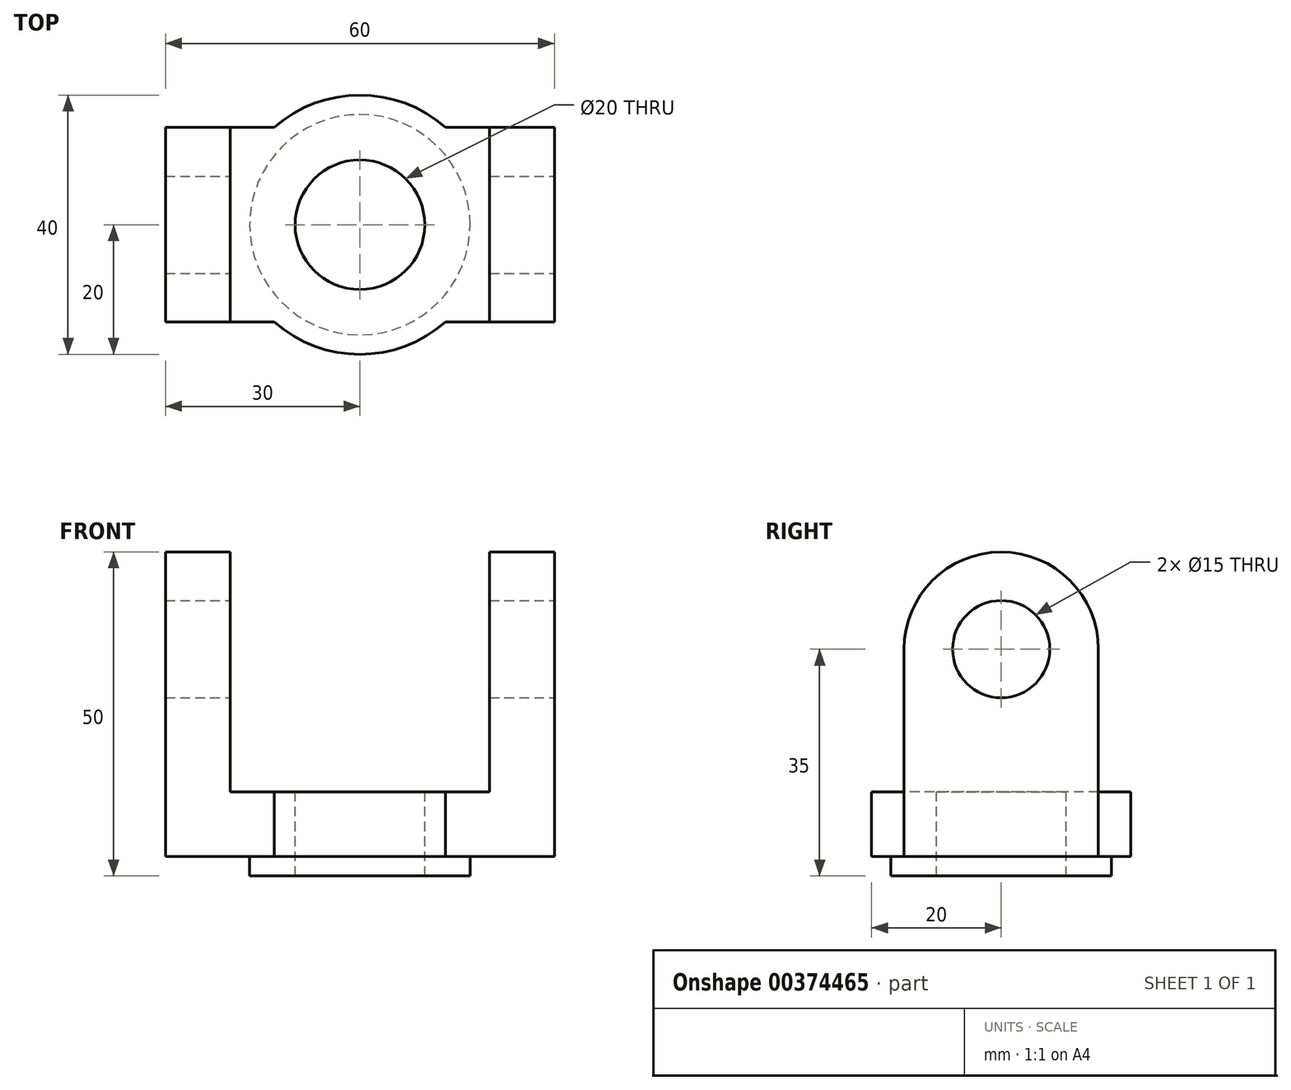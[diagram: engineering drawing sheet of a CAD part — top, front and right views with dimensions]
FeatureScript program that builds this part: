
annotation { "Feature Type Name" : "Feature", "Feature Type Description" : "" }
export const myFeature = defineFeature(function(context is Context, id is Id, definition is map)
    precondition{}
    {
        {
            var Q0;
            Q0=qCreatedBy(makeId("Front.planeOp"),FACE);
            var sketch = newSketch(context, id + "F0", { "sketchPlane" : qUnion([Q0])});
            skLineSegment(sketch, "E0", {"start": v(0, 0) * mm, "end": v(60, 0) * mm});
            skLineSegment(sketch, "E1", {"start": v(60, 0) * mm, "end": v(60, 10) * mm});
            skLineSegment(sketch, "E2", {"start": v(60, 10) * mm, "end": v(0, 10) * mm});
            skLineSegment(sketch, "E3", {"start": v(0, 10) * mm, "end": v(0, 0) * mm});
            skSolve(sketch);
        }
        {
            var Q0;
            Q0 = qSketchRegion(id + "F0", true);
            extrude(context, id + "F1", {"entities" : qUnion([Q0]), "depth" : 30 * mm});
        }
        {
            var Q0;
            Q0=makeQuery(id+"F1.opExtrude","SWEPT_FACE",FACE,{"disambiguationData":[OSD([sQuery(id+"F0.wireOp",EDGE,"E0")])]});
            var sketch = newSketch(context, id + "F2", { "sketchPlane" : qUnion([Q0])});
            skLineSegment(sketch, "E4.0.0", {"start": v(0, 0) * mm, "end": v(60, 0) * mm});
            skLineSegment(sketch, "E4.0.1", {"start": v(60, 0) * mm, "end": v(60, 30) * mm});
            skLineSegment(sketch, "E4.0.2", {"start": v(60, 30) * mm, "end": v(0, 30) * mm});
            skLineSegment(sketch, "E4.0.3", {"start": v(0, 30) * mm, "end": v(0, 0) * mm});
            skLineSegment(sketch, "E5", {"start": v(0, 15) * mm, "end": v(60, 15) * mm, "construction": true});
            skCircle(sketch, "E6", {"center": v(30, 15) * mm, "radius": 17 * mm});
            skSolve(sketch);
        }
        {
            var Q0;
            Q0=makeQuery(id+"F2.imprint","IMPRINT",FACE,{"disambiguationData":[TD([[makeQuery(id+"F2.imprint","IMPRINT",EDGE,{"derivedFrom":sQuery(id+"F2.wireOp",EDGE,"E6")}),1.0]])]});
            extrude(context, id + "F3", {"entities" : qUnion([Q0]), "operationType" : NewBodyOperationType.ADD, "depth" : 3 * mm});
        }
        {
            var Q0;
            Q0=makeQuery(id+"F1.opExtrude","SWEPT_FACE",FACE,{"disambiguationData":[OSD([sQuery(id+"F0.wireOp",EDGE,"E2")])]});
            var sketch = newSketch(context, id + "F4", { "sketchPlane" : qUnion([Q0])});
            skLineSegment(sketch, "E7", {"start": v(0, -15) * mm, "end": v(60, -15) * mm, "construction": true});
            skCircle(sketch, "E8", {"center": v(30, -15) * mm, "radius": 20 * mm});
            skLineSegment(sketch, "E9.0.0", {"start": v(60, 0) * mm, "end": v(0, 0) * mm});
            skLineSegment(sketch, "E9.0.1", {"start": v(0, 0) * mm, "end": v(0, -30) * mm});
            skLineSegment(sketch, "E9.0.2", {"start": v(0, -30) * mm, "end": v(60, -30) * mm});
            skLineSegment(sketch, "E9.0.3", {"start": v(60, -30) * mm, "end": v(60, 0) * mm});
            skSolve(sketch);
        }
        {
            var Q0;
            {var subQ0=sQuery(id+"F4.wireOp",EDGE,"E9.0.0");var subQ1=sQuery(id+"F4.wireOp",EDGE,"E8");var subQ2=makeQuery(id+"F4.imprint","INTERSECT",VERTEX,{"disambiguationData":[OD(0.0)],"derivedFrom":[subQ1,subQ0]});Q0=makeQuery(id+"F4.imprint","IMPRINT",FACE,{"disambiguationData":[TD([[makeQuery(id+"F4.imprint","IMPRINT",EDGE,{"disambiguationData":[TD([[subQ2,1.0]])],"derivedFrom":subQ1}),1.0]])]});}
            var Q1;
            {var subQ0=sQuery(id+"F4.wireOp",EDGE,"E9.0.2");var subQ1=sQuery(id+"F4.wireOp",EDGE,"E8");var subQ2=makeQuery(id+"F4.imprint","INTERSECT",VERTEX,{"disambiguationData":[OD(0.0)],"derivedFrom":[subQ1,subQ0]});Q1=makeQuery(id+"F4.imprint","IMPRINT",FACE,{"disambiguationData":[TD([[makeQuery(id+"F4.imprint","IMPRINT",EDGE,{"disambiguationData":[TD([[subQ2,-1.0]])],"derivedFrom":subQ1}),1.0]])]});}
            extrude(context, id + "F5", {"entities" : qUnion([Q0, Q1]), "operationType" : NewBodyOperationType.ADD, "oppositeDirection" : true, "depth" : 10 * mm});
        }
        {
            var Q0;
            {var subQ0=sQuery(id+"F4.wireOp",EDGE,"E8");Q0=makeQuery(id+"F5.boolean.opBoolean","MERGE",FACE,{"derivedFrom":[makeQuery(id+"F1.opExtrude","SWEPT_FACE",FACE,{"disambiguationData":[OSD([sQuery(id+"F0.wireOp",EDGE,"E2")])]}),makeQuery(id+"F5.opExtrude","CAP_FACE",FACE,{"disambiguationData":[OSD([subQ0,sQuery(id+"F4.wireOp",EDGE,"E9.0.0")])],"isStart":true}),makeQuery(id+"F5.opExtrude","CAP_FACE",FACE,{"disambiguationData":[OSD([subQ0,sQuery(id+"F4.wireOp",EDGE,"E9.0.2")])],"isStart":true})]});}
            var sketch = newSketch(context, id + "F6", { "sketchPlane" : qUnion([Q0])});
            skLineSegment(sketch, "E10", {"start": v(0, -15) * mm, "end": v(60, -15) * mm, "construction": true});
            skCircle(sketch, "E11", {"center": v(30, -15) * mm, "radius": 10 * mm});
            skSolve(sketch);
        }
        {
            var Q0;
            Q0 = qSketchRegion(id + "F6", true);
            extrude(context, id + "F7", {"entities" : qUnion([Q0]), "operationType" : NewBodyOperationType.REMOVE, "oppositeDirection" : true, "depth" : 25 * mm});
        }
        {
            var Q0;
            Q0=makeQuery(id+"F3.opExtrude","CAP_FACE",FACE,{"disambiguationData":[OSD([sQuery(id+"F2.wireOp",EDGE,"E4.0.0"),sQuery(id+"F2.wireOp",EDGE,"E4.0.2"),sQuery(id+"F2.wireOp",EDGE,"E6")])],"isStart":false});
            var sketch = newSketch(context, id + "F8", { "sketchPlane" : qUnion([Q0])});
            skCircle(sketch, "E12", {"center": v(30, 15) * mm, "radius": 17 * mm});
            skCircle(sketch, "E13.0", {"center": v(30, 15) * mm, "radius": 10 * mm});
            skLineSegment(sketch, "E14.0.0", {"start": v(38, 30) * mm, "end": v(22, 30) * mm});
            skArc(sketch, "E14.0.1", {"start": v(22, 30) * mm, "mid": v(13, 15) * mm, "end": v(22, 0) * mm});
            skLineSegment(sketch, "E14.0.2", {"start": v(22, 0) * mm, "end": v(38, 0) * mm});
            skArc(sketch, "E14.0.3", {"start": v(38, 0) * mm, "mid": v(47, 15) * mm, "end": v(38, 30) * mm});
            skSolve(sketch);
        }
        {
            var Q0;
            {var subQ0=sQuery(id+"F8.wireOp",EDGE,"E14.0.0");Q0=makeQuery(id+"F8.imprint","IMPRINT",FACE,{"disambiguationData":[TD([[makeQuery(id+"F8.imprint","IMPRINT",EDGE,{"derivedFrom":subQ0}),1.0]])]});}
            var Q1;
            {var subQ0=sQuery(id+"F8.wireOp",EDGE,"E14.0.2");Q1=makeQuery(id+"F8.imprint","IMPRINT",FACE,{"disambiguationData":[TD([[makeQuery(id+"F8.imprint","IMPRINT",EDGE,{"derivedFrom":subQ0}),-1.0]])]});}
            extrude(context, id + "F9", {"entities" : qUnion([Q0, Q1]), "operationType" : NewBodyOperationType.ADD, "oppositeDirection" : true, "depth" : 3 * mm});
        }
        {
            var Q0;
            {var subQ0=sQuery(id+"F4.wireOp",EDGE,"E8");Q0=makeQuery(id+"F5.boolean.opBoolean","MERGE",FACE,{"derivedFrom":[makeQuery(id+"F1.opExtrude","SWEPT_FACE",FACE,{"disambiguationData":[OSD([sQuery(id+"F0.wireOp",EDGE,"E2")])]}),makeQuery(id+"F5.opExtrude","CAP_FACE",FACE,{"disambiguationData":[OSD([subQ0,sQuery(id+"F4.wireOp",EDGE,"E9.0.0")])],"isStart":true}),makeQuery(id+"F5.opExtrude","CAP_FACE",FACE,{"disambiguationData":[OSD([subQ0,sQuery(id+"F4.wireOp",EDGE,"E9.0.2")])],"isStart":true})]});}
            var sketch = newSketch(context, id + "F10", { "sketchPlane" : qUnion([Q0])});
            skLineSegment(sketch, "E15.0.0", {"start": v(60, 0) * mm, "end": v(43.23, 0) * mm});
            skArc(sketch, "E15.0.1", {"start": v(43.23, 0) * mm, "mid": v(30, 5) * mm, "end": v(16.77, 0) * mm});
            skLineSegment(sketch, "E15.0.2", {"start": v(16.77, 0) * mm, "end": v(0, 0) * mm});
            skLineSegment(sketch, "E15.0.3", {"start": v(0, 0) * mm, "end": v(0, -30) * mm});
            skLineSegment(sketch, "E15.0.4", {"start": v(0, -30) * mm, "end": v(16.77, -30) * mm});
            skArc(sketch, "E15.0.5", {"start": v(16.77, -30) * mm, "mid": v(30, -35) * mm, "end": v(43.23, -30) * mm});
            skLineSegment(sketch, "E15.0.6", {"start": v(43.23, -30) * mm, "end": v(60, -30) * mm});
            skLineSegment(sketch, "E15.0.7", {"start": v(60, -30) * mm, "end": v(60, 0) * mm});
            skLineSegment(sketch, "E16", {"start": v(0, 0) * mm, "end": v(10, 0) * mm});
            skLineSegment(sketch, "E17", {"start": v(10, 0) * mm, "end": v(10, -30) * mm});
            skLineSegment(sketch, "E18", {"start": v(10, -30) * mm, "end": v(0, -30) * mm});
            skLineSegment(sketch, "E19", {"start": v(60, 0) * mm, "end": v(50, 0) * mm});
            skLineSegment(sketch, "E20", {"start": v(50, 0) * mm, "end": v(50, -30) * mm});
            skLineSegment(sketch, "E21", {"start": v(50, -30) * mm, "end": v(60, -30) * mm});
            skSolve(sketch);
        }
        {
            var Q0;
            Q0=makeQuery(id+"F10.imprint","IMPRINT",FACE,{"disambiguationData":[TD([[makeQuery(id+"F10.imprint","IMPRINT",EDGE,{"derivedFrom":sQuery(id+"F10.wireOp",EDGE,"E15.0.3")}),-1.0]])]});
            var Q1;
            Q1=makeQuery(id+"F10.imprint","IMPRINT",FACE,{"disambiguationData":[TD([[makeQuery(id+"F10.imprint","IMPRINT",EDGE,{"derivedFrom":sQuery(id+"F10.wireOp",EDGE,"E15.0.7")}),1.0]])]});
            extrude(context, id + "F11", {"entities" : qUnion([Q0, Q1]), "operationType" : NewBodyOperationType.ADD, "depth" : (35 - 13) * mm});
        }
        {
            var Q0;
            Q0=makeQuery(id+"F11.boolean.opBoolean","MERGE",FACE,{"derivedFrom":[makeQuery(id+"F1.opExtrude","SWEPT_FACE",FACE,{"disambiguationData":[OSD([sQuery(id+"F0.wireOp",EDGE,"E3")])]}),makeQuery(id+"F11.opExtrude","SWEPT_FACE",FACE,{"disambiguationData":[OSD([sQuery(id+"F10.wireOp",EDGE,"E15.0.3")])]})]});
            var sketch = newSketch(context, id + "F12", { "sketchPlane" : qUnion([Q0])});
            skCircle(sketch, "E22", {"center": v(15, 32) * mm, "radius": 15 * mm});
            skSolve(sketch);
        }
        {
            var Q0;
            Q0 = qSketchRegion(id + "F12", true);
            extrude(context, id + "F13", {"entities" : qUnion([Q0]), "operationType" : NewBodyOperationType.ADD, "oppositeDirection" : true, "depth" : 10 * mm});
        }
        {
            var Q0;
            Q0=makeQuery(id+"F11.boolean.opBoolean","MERGE",FACE,{"derivedFrom":[makeQuery(id+"F1.opExtrude","SWEPT_FACE",FACE,{"disambiguationData":[OSD([sQuery(id+"F0.wireOp",EDGE,"E1")])]}),makeQuery(id+"F11.opExtrude","SWEPT_FACE",FACE,{"disambiguationData":[OSD([sQuery(id+"F10.wireOp",EDGE,"E15.0.7")])]})]});
            var sketch = newSketch(context, id + "F14", { "sketchPlane" : qUnion([Q0])});
            skCircle(sketch, "E23", {"center": v(-15, 32) * mm, "radius": 15 * mm});
            skSolve(sketch);
        }
        {
            var Q0;
            Q0 = qSketchRegion(id + "F14", true);
            extrude(context, id + "F15", {"entities" : qUnion([Q0]), "operationType" : NewBodyOperationType.ADD, "oppositeDirection" : true, "depth" : 10 * mm});
        }
        {
            var Q0;
            Q0=makeQuery(id+"F15.boolean.opBoolean","MERGE",FACE,{"derivedFrom":[makeQuery(id+"F11.boolean.opBoolean","MERGE",FACE,{"derivedFrom":[makeQuery(id+"F1.opExtrude","SWEPT_FACE",FACE,{"disambiguationData":[OSD([sQuery(id+"F0.wireOp",EDGE,"E1")])]}),makeQuery(id+"F11.opExtrude","SWEPT_FACE",FACE,{"disambiguationData":[OSD([sQuery(id+"F10.wireOp",EDGE,"E15.0.7")])]})]}),makeQuery(id+"F15.opExtrude","CAP_FACE",FACE,{"disambiguationData":[OSD([sQuery(id+"F14.wireOp",EDGE,"E23")])],"isStart":true})]});
            var sketch = newSketch(context, id + "F16", { "sketchPlane" : qUnion([Q0])});
            skCircle(sketch, "E24", {"center": v(-15, 32) * mm, "radius": 7.5 * mm});
            skSolve(sketch);
        }
        {
            var Q0;
            Q0 = qSketchRegion(id + "F16", true);
            extrude(context, id + "F17", {"entities" : qUnion([Q0]), "operationType" : NewBodyOperationType.REMOVE, "oppositeDirection" : true, "depth" : 60 * mm});
        }
    });
